# Revit family: Qwik Pak LS assembly
name_source: partatom
category: Mechanical Equipment
revit_build: Autodesk Revit 2013 (Build: 20120221_2030(x64)
units: mm (PartAtom-declared; Revit-internal decimal feet)

## types (4) — shared parameters
2" Cast Iron Check Valve (30-0152) = Yes
2" PVC Ball Valve w/ Extension Handle = Yes
2" PVC SCH 40 Discharge Pipe = Yes
3/4" Galvanized Slide Rail Pipe = Yes
4" Pipe Seal Inlet Hub = Yes
ATS URL = http://www.atsspec.net
Assembly Code = F1050
CW Connection = Yes
Default Elevation = 0"
Fiberglass Basin w/AFD = Yes
Fiberglass Cover = Yes
HW Connection = No
Length = 6"
Manufacturer = Zoeller
Masterformat Number = 33 44 13.13
Masterformat Title = Catchbasins
Material = Glass-Zoeller-Fiberglass
Omniclass Table 23 Code = 23.60.30.00
Omniclass Table 23 Title = General Pipework and Ductwork Products
PVC Float Tree & 3-15' Float Switches (Mechanical) - Non-Mercury = Yes
Price = Prices may vary. Please consult Manufacturer Representative for most up-to-date price list.
Product Documentation Link = http://cdn.qleapahead.com
Product Page URL = http://www.zoellerpumps.com
URL = http://www.zoellerpumps.com
Vent Connection = No
Waste Connection = No
Width = 30 1/4"
Z Rail Disconnect System w/ 2" Discharge = Yes

## per-type parameters (varying)
| type | Connection Diameter | Connection Radius | Connector Description | Description | Height | Model | Rail Slide Assembly Kit |
| 35-0068_24x60_Simplex_Fiberglass_Basin_Assembly_1.25" | 1 1/4" | 5/8" | 1.25" Pump Connection | Fiber Glass Basin. 24" x 60". Fiberglass basin. Fiberglass Anti-Flotation ring. Fiberglass cover. Z-Rail disconnect system with 2" discharge. Ductile Iron construction. 3/4" galvanized slide rail pipe. 2" PVC Sch 4- discharge pipe. 2" Cast iron check valve (30-0152) 2" PVC ball valve w/ extension handle. 4" Pipe seal inlet hub. PVC Float tree & 3-15' float switches (mechanical-non mercury). | 60" | 35-0068 | Rail_Slide_Assembly-Kit-10-366x_Zoeller : 10-3663_1.25"_Pump_Connection |
| 35-0069_24x84_Simplex_Fiberglass_Basin_Assembly_1.25" | 1 1/4" | 5/8" | 1.25" Pump Connection | Fiber Glass Basin. 24" x 84"  Fiberglass basin. Fiberglass Anti-Flotation ring. Fiberglass cover. Z-Rail disconnect system with 2" discharge. Ductile Iron construction. 3/4" galvanized slide rail pipe. 2" PVC Sch 4- discharge pipe. 2" Cast iron check valve (30-0152) 2" PVC ball valve w/ extension handle. 4" Pipe seal inlet hub. PVC Float tree & 3-15' float switches (mechanical-non mercury). | 84" | 35-0069 | Rail_Slide_Assembly-Kit-10-366x_Zoeller : 10-3663_1.25"_Pump_Connection |
| 35-0068_24x60_Simplex_Fiberglass_Basin_Assembly_2" | 2" | 1" | 2" Pump Connection | Fiber Glass Basin. 24" x 60". Fiberglass basin. Fiberglass Anti-Flotation ring. Fiberglass cover. Z-Rail disconnect system with 2" discharge. Ductile Iron construction. 3/4" galvanized slide rail pipe. 2" PVC Sch 4- discharge pipe. 2" Cast iron check valve (30-0152) 2" PVC ball valve w/ extension handle. 4" Pipe seal inlet hub. PVC Float tree & 3-15' float switches (mechanical-non mercury). | 60" | 35-0068 | Rail_Slide_Assembly-Kit-10-366x_Zoeller : 10-3664_2"_Pump_Connection |
| 35-0069_24x84_Simplex_Fiberglass_Basin_Assembly_2" | 2" | 1" | 2" Pump Connection | Fiber Glass Basin. 24" x 84"  Fiberglass basin. Fiberglass Anti-Flotation ring. Fiberglass cover. Z-Rail disconnect system with 2" discharge. Ductile Iron construction. 3/4" galvanized slide rail pipe. 2" PVC Sch 4- discharge pipe. 2" Cast iron check valve (30-0152) 2" PVC ball valve w/ extension handle. 4" Pipe seal inlet hub. PVC Float tree & 3-15' float switches (mechanical-non mercury). | 84" | 35-0069 | Rail_Slide_Assembly-Kit-10-366x_Zoeller : 10-3664_2"_Pump_Connection |

## geometry (parser evidence)
native form markers: Blend x30, Sweep x4
no freeform markers — native parametric forms only
